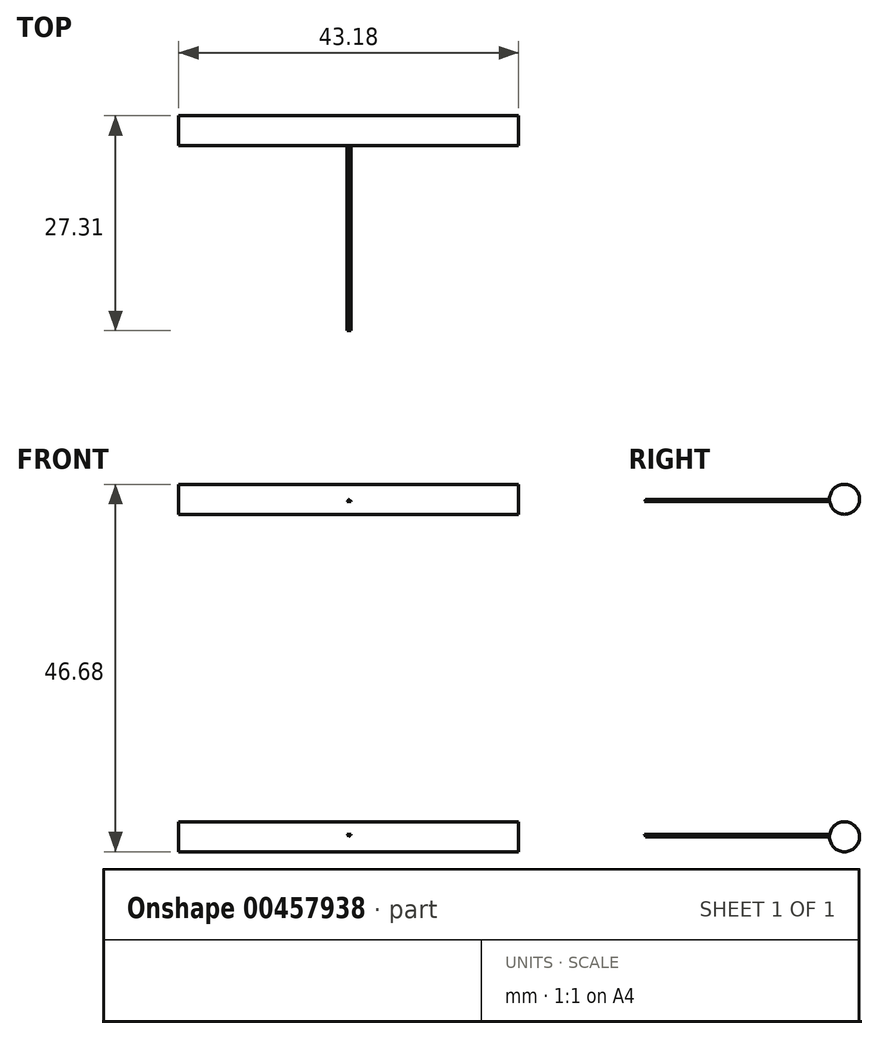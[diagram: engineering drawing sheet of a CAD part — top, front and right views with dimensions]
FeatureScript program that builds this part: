
annotation { "Feature Type Name" : "Feature", "Feature Type Description" : "" }
export const myFeature = defineFeature(function(context is Context, id is Id, definition is map)
    precondition{}
    {
        {
            var Q0;
            Q0=qCreatedBy(makeId("Front.planeOp"),FACE);
            var sketch = newSketch(context, id + "F0", { "sketchPlane" : qUnion([Q0])});
            skLineSegment(sketch, "E0.bottom", {"start": v(-21.44, 21.44) * mm, "end": v(21.44, 21.44) * mm});
            skLineSegment(sketch, "E0.top", {"start": v(-21.44, -21.44) * mm, "end": v(21.44, -21.44) * mm});
            skLineSegment(sketch, "E0.left", {"start": v(-21.44, 21.44) * mm, "end": v(-21.44, -21.44) * mm});
            skLineSegment(sketch, "E0.right", {"start": v(21.44, 21.44) * mm, "end": v(21.44, -21.44) * mm});
            skPoint(sketch, "E0.middle", {"position": v(0, 0) * mm});
            skCircle(sketch, "E1", {"center": v(0, 0) * mm, "radius": 10.72 * mm});
            skSolve(sketch);
        }
        {
            var Q0;
            Q0=makeQuery(id+"F0.imprint","IMPRINT",FACE,{"disambiguationData":[TD([[makeQuery(id+"F0.imprint","IMPRINT",EDGE,{"derivedFrom":sQuery(id+"F0.wireOp",EDGE,"E0.bottom")}),-1.0]])]});
            extrude(context, id + "F1", {"entities" : qUnion([Q0]), "depth" : 25.4 * mm, "offsetDistance" : 25.4 * mm});
        }
        {
            var Q0;
            Q0=makeQuery(id+"F1.opExtrude","CAP_FACE",FACE,{"disambiguationData":[OSD([sQuery(id+"F0.wireOp",EDGE,"E0.bottom"),sQuery(id+"F0.wireOp",EDGE,"E0.top"),sQuery(id+"F0.wireOp",EDGE,"E0.left"),sQuery(id+"F0.wireOp",EDGE,"E0.right"),sQuery(id+"F0.wireOp",EDGE,"E1")])],"isStart":false});
            var sketch = newSketch(context, id + "F2", { "sketchPlane" : qUnion([Q0])});
            skFitSpline(sketch, "E2.MirrorC", {"points": [v(0, -21.44) * mm, v(-31.8, -40.34) * mm, v(-17.9, -101.47) * mm, v(-24.58, -66.76) * mm, v(-14.18, -69.87) * mm, v(-23.15, -57.45) * mm, v(21.44, -85.42) * mm, v(-17.46, -47.72) * mm, v(9.77, -59.73) * mm, v(-11.7, -36.11) * mm, v(0, -21.44) * mm]});
            skFitSpline(sketch, "E3.MirrorC", {"points": [v(0, -21.44) * mm, v(10.1, -51.1) * mm, v(56.97, -85.03) * mm, v(23.52, -53.99) * mm, v(53.05, -53.56) * mm, v(16.41, -38.66) * mm, v(46.61, -40.4) * mm, v(14.47, -25.9) * mm, v(0, -21.44) * mm]});
            skLineSegment(sketch, "E4.0", {"start": v(-21.44, -21.44) * mm, "end": v(-6.5, -21.44) * mm});
            skLineSegment(sketch, "E5.trimOffspring", {"start": v(4.65, -21.44) * mm, "end": v(21.44, -21.44) * mm});
            skLineSegment(sketch, "E6", {"start": v(-0.18, -21.15) * mm, "end": v(0.33, -21.15) * mm});
            skSolve(sketch);
        }
        {
            var Q0;
            {var subQ4=sQuery(id+"F2.wireOp",EDGE,"E2.MirrorC");var subQ6=makeQuery(id+"F2.imprint","IMPRINT",VERTEX,{"derivedFrom":subQ4});Q0=makeQuery(id+"F2.imprint","IMPRINT",FACE,{"disambiguationData":[TD([[makeQuery(id+"F2.imprint","IMPRINT",EDGE,{"disambiguationData":[TD([[subQ6,-1.0]])],"derivedFrom":subQ4}),1.0]])]});}
            var Q1;
            {var subQ0=sQuery(id+"F2.wireOp",EDGE,"E6");Q1=makeQuery(id+"F2.imprint","IMPRINT",FACE,{"disambiguationData":[TD([[makeQuery(id+"F2.imprint","IMPRINT",EDGE,{"derivedFrom":subQ0}),-1.0]])]});}
            extrude(context, id + "F3", {"entities" : qUnion([Q0, Q1]), "depth" : 25.4 * mm, "offsetDistance" : 25.4 * mm});
        }
        {
            var Q0;
            Q0=makeQuery(id+"F1.opExtrude","SWEPT_FACE",FACE,{"disambiguationData":[OSD([sQuery(id+"F0.wireOp",EDGE,"E0.left")])]});
            var sketch = newSketch(context, id + "F4", { "sketchPlane" : qUnion([Q0])});
            skLineSegment(sketch, "E7.bottom", {"start": v(25.4, 21.44) * mm, "end": v(0, 21.44) * mm});
            skLineSegment(sketch, "E7.top", {"start": v(25.4, -21.44) * mm, "end": v(0, -21.44) * mm});
            skLineSegment(sketch, "E7.left", {"start": v(25.4, 21.44) * mm, "end": v(25.4, -21.44) * mm});
            skLineSegment(sketch, "E7.right", {"start": v(0, 21.44) * mm, "end": v(0, -21.44) * mm});
            skSolve(sketch);
        }
        {
            var Q0;
            Q0 = qSketchRegion(id + "F4", true);
            extrude(context, id + "F5", {"entities" : qUnion([Q0]), "operationType" : NewBodyOperationType.REMOVE, "oppositeDirection" : true, "depth" : 74.68 * mm, "offsetDistance" : 25.4 * mm});
        }
        {
            var Q0;
            Q0=qCreatedBy(makeId("Right.planeOp"),FACE);
            var sketch = newSketch(context, id + "F6", { "sketchPlane" : qUnion([Q0])});
            skPoint(sketch, "E8.0", {"position": v(-25.4, -21.44) * mm});
            skCircle(sketch, "E9", {"center": v(-25.4, -21.44) * mm, "radius": 1.9 * mm});
            skSolve(sketch);
        }
        {
            var Q0;
            Q0 = qSketchRegion(id + "F6", true);
            extrude(context, id + "F7", {"entities" : qUnion([Q0]), "operationType" : NewBodyOperationType.ADD, "endBound" : BoundingType.SYMMETRIC, "depth" : 43.18 * mm, "offsetDistance" : 25.4 * mm});
        }
        {
            var Q0;
            Q0=makeQuery(id+"F7.opExtrude","CAP_FACE",FACE,{"disambiguationData":[OSD([sQuery(id+"F6.wireOp",EDGE,"E9")])],"isStart":true});
            cPlane(context, id + "F8", {"entities" : qUnion([Q0]), "cplaneType" : CPlaneType.OFFSET, "offset" : 0 * mm, "oppositeDirection" : true, "width" : 152.4 * mm, "height" : 152.4 * mm});
        }
        {
            var Q0;
            Q0=qCreatedBy(id+"F8.planeOp",FACE);
            var sketch = newSketch(context, id + "F9", { "sketchPlane" : qUnion([Q0])});
            skPoint(sketch, "E10.0", {"position": v(50.8, -21.15) * mm});
            skPoint(sketch, "E11.0", {"position": v(50.8, -83.59) * mm});
            skPoint(sketch, "E12.0", {"position": v(25.4, -85.42) * mm});
            skPoint(sketch, "E13.0", {"position": v(25.4, -36.11) * mm});
            skArc(sketch, "E14", {"start": v(25.4, -85.42) * mm, "mid": v(32.51, -60.77) * mm, "end": v(25.4, -36.11) * mm});
            skArc(sketch, "E15", {"start": v(50.8, -21.15) * mm, "mid": v(42.9, -52.37) * mm, "end": v(50.8, -83.59) * mm});
            skArc(sketch, "E16", {"start": v(25.4, -101.49) * mm, "mid": v(40.44, -95.86) * mm, "end": v(50.8, -83.59) * mm});
            skArc(sketch, "E17", {"start": v(25.4, -101.49) * mm, "mid": v(28.26, -93.46) * mm, "end": v(25.4, -85.42) * mm});
            skLineSegment(sketch, "E18", {"start": v(50.8, -21.15) * mm, "end": v(50.8, -83.59) * mm});
            skLineSegment(sketch, "E19", {"start": v(50.8, -108.98) * mm, "end": v(25.4, -101.49) * mm});
            skLineSegment(sketch, "E20", {"start": v(25.4, -85.42) * mm, "end": v(25.4, -101.49) * mm});
            skLineSegment(sketch, "E21", {"start": v(25.4, -85.42) * mm, "end": v(25.4, -36.11) * mm});
            skLineSegment(sketch, "E22", {"start": v(50.8, -108.98) * mm, "end": v(50.8, -83.59) * mm});
            skSolve(sketch);
        }
        {
            var Q0;
            Q0 = qSketchRegion(id + "F9", true);
            extrude(context, id + "F10", {"entities" : qUnion([Q0]), "operationType" : NewBodyOperationType.REMOVE, "endBound" : BoundingType.SYMMETRIC, "oppositeDirection" : true, "depth" : 248.4 * mm, "offsetDistance" : 25.4 * mm});
        }
        {
            var Q0;
            Q0=makeQuery(id+"F10.boolean.opBoolean","SPLIT",BODY,{"disambiguationData":[OD(1.0)],"derivedFrom":makeQuery(id+"F3.opExtrude","SWEPT_BODY",BODY,{"disambiguationData":[OSD([sQuery(id+"F2.wireOp",EDGE,"E2.MirrorC"),sQuery(id+"F2.wireOp",EDGE,"E3.MirrorC"),sQuery(id+"F2.wireOp",EDGE,"E6")])]})});
            var Q1;
            Q1=qCreatedBy(makeId("Top.planeOp"),FACE);
            mirror(context, id + "F11", {"entities" : qUnion([Q0]), "mirrorPlane" : qUnion([Q1])});
        }
    });
